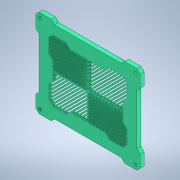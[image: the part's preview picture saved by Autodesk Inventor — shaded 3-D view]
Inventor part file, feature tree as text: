
AUTODESK INVENTOR PART (.ipt)
format: ipt  version: 2020 (Build 240168000, 168)  size: 755,200 bytes
history: native  units: mm
features: reference x26, sketch x5, other x4, extrude x3, projected_geometry x3, hole x1
ambient origin geometry x8: Origin, YZ Plane, XZ Plane, XY Plane, X Axis, Y Axis, Z Axis, Center Point
bodies: Solid1 (feature_tree)
feature tree (42):
  extrude  "Extrusion1"  Depth=2.0mm TaperAngle=0.0deg
  extrude  "Extrusion2"  Depth=5.0mm
  hole  "Hole1"  [1 undecoded]
  other  "Grill1"
  extrude  "Extrusion3"  Depth=10.0mm
  sketch  "Sketch1"  dims[d0=3.0mm d1=0.0mm d2=2.0mm d3=0.0mm]
  reference  "Reference1"
  reference  "Reference2"
  reference  "Reference3"
  reference  "Reference4"
  reference  "Reference5"
  reference  "Reference6"
  reference  "Reference7"
  reference  "Reference8"
  reference  "Reference9"
  reference  "Reference10"
  reference  "Reference11"
  reference  "Reference12"
  reference  "Reference13"
  reference  "Reference14"
  reference  "Reference15"
  reference  "Reference16"
  reference  "Reference17"
  reference  "Reference18"
  reference  "Reference19"
  reference  "Reference20"
  reference  "Reference21"
  reference  "Reference22"
  reference  "Reference23"
  reference  "Reference24"
  sketch  "Sketch2"  dims[d4=3.4mm d5=6.0mm d6=11.0mm d7=2.6mm d8=90.0deg d9=5.0mm d10=0.0mm d56=5.0mm]
  reference  "Reference25"
  sketch  "Sketch3"  dims[d57=5.0mm d58=5.0mm]
  reference  "Reference26"
  sketch  "Sketch5"  dims[d59=5.0mm d60=10.0mm]
  projected_geometry  "Projected Loop3"
  projected_geometry  "Projected Loop4"
  sketch  "Sketch6"  dims[d61=10.0mm d62=10.0mm d63=10.0mm d65=18.0mm d66=18.0mm d67=18.0mm d81=1.5mm d82=3.0mm d83=0.0mm d84=5.0mm d85=3.0mm d86=0.0mm d87=1.5mm d88=0.0mm d89=0.0mm d90=1.0mm d91=0.0mm d92=0.0mm d93=0.0mm d94=294.859876mm d95=5.0mm d96=4.0mm d97=4.0mm d98=4.0mm d99=4.0mm d100=4.0mm d101=4.0mm d102=4.0mm d103=4.0mm d104=4.0mm d105=4.0mm d106=4.0mm d107=4.0mm d108=4.0mm d109=0.2mm d110=2.0mm d111=0.0mm]
  projected_geometry  "Projected Loop5"
  other  "Assembly2"
  other  "Assembly2.iam"
  other  "Case:1"
note: 1 required parameter value undecoded (feature->parameter linkage not recoverable at this tier; creation-order binding heuristic only, values carry confidence <= 0.55)
